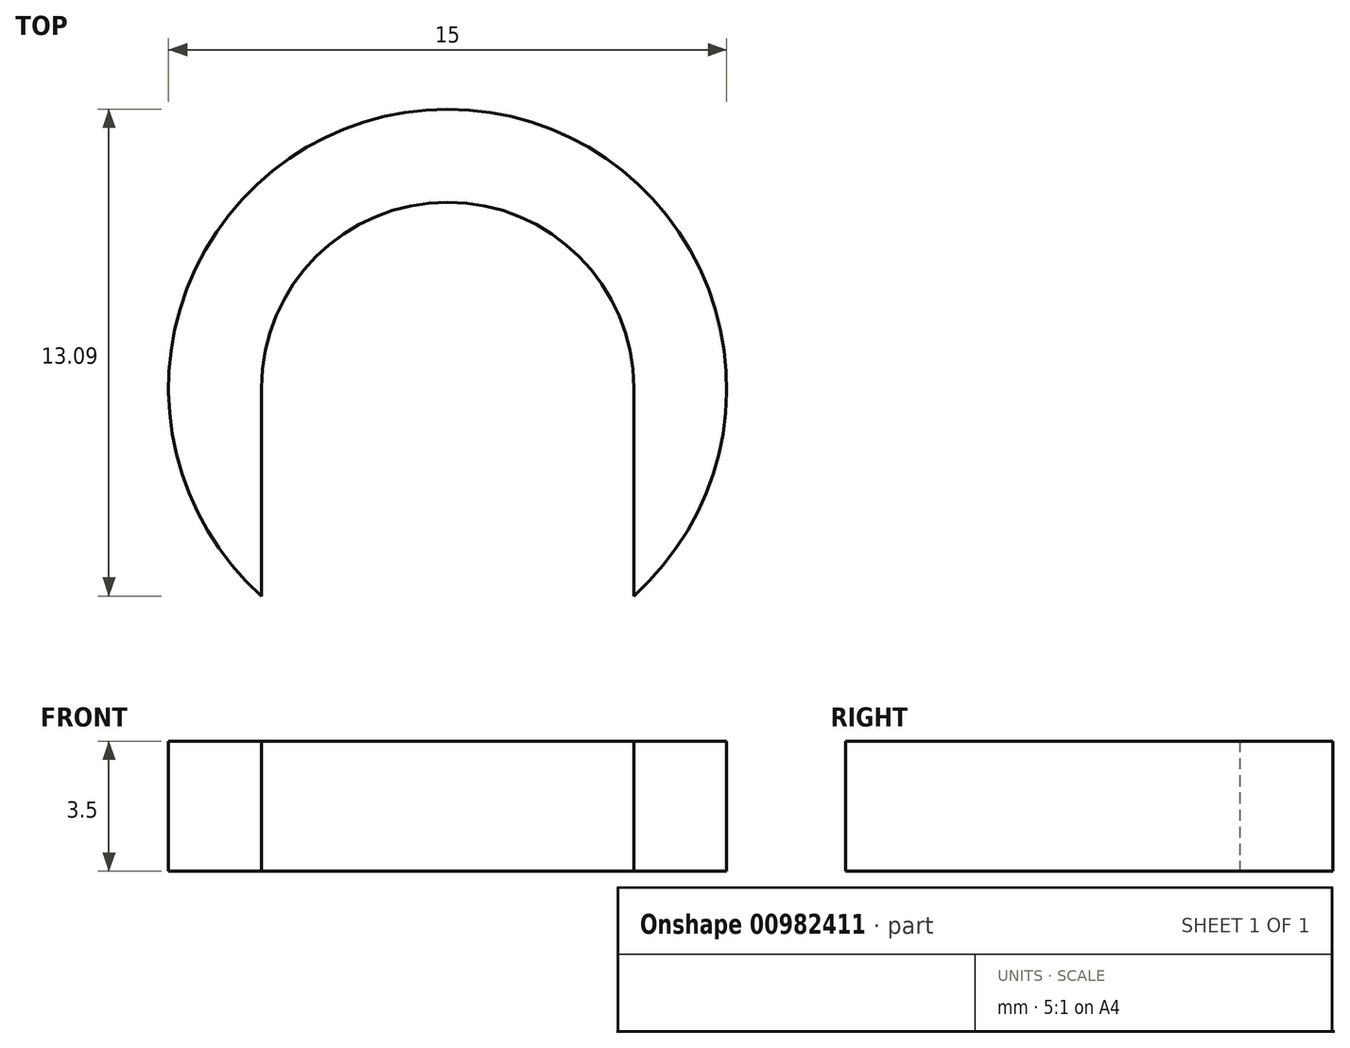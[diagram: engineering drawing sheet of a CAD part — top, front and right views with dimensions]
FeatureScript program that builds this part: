
annotation { "Feature Type Name" : "Feature", "Feature Type Description" : "" }
export const myFeature = defineFeature(function(context is Context, id is Id, definition is map)
    precondition{}
    {
        {
            var Q0;
            Q0=qCreatedBy(makeId("Top.planeOp"),FACE);
            var sketch = newSketch(context, id + "F0", { "sketchPlane" : qUnion([Q0])});
            skCircle(sketch, "E0", {"center": v(0, 0) * mm, "radius": 7.5 * mm});
            skSolve(sketch);
        }
        {
            var Q0;
            Q0=qCreatedBy(makeId("Top.planeOp"),FACE);
            var sketch = newSketch(context, id + "F1", { "sketchPlane" : qUnion([Q0])});
            skLineSegment(sketch, "E1", {"start": v(0, -7.56) * mm, "end": v(-5, -7.56) * mm});
            skLineSegment(sketch, "E2", {"start": v(0, -7.56) * mm, "end": v(5, -7.56) * mm});
            skLineSegment(sketch, "E3", {"start": v(5, -7.56) * mm, "end": v(5, 0) * mm});
            skLineSegment(sketch, "E4", {"start": v(-5, -7.56) * mm, "end": v(-5, 0) * mm});
            skArc(sketch, "E5", {"start": v(5, 0) * mm, "mid": v(0, 5) * mm, "end": v(-5, 0) * mm});
            skSolve(sketch);
        }
        {
            var Q0;
            Q0=makeQuery(id+"F0.imprint","IMPRINT",FACE,{"disambiguationData":[TD([[makeQuery(id+"F0.imprint","IMPRINT",EDGE,{"derivedFrom":sQuery(id+"F0.wireOp",EDGE,"E0")}),1.0]])]});
            extrude(context, id + "F2", {"entities" : qUnion([Q0]), "depth" : 3.5 * mm, "offsetDistance" : 25 * mm});
        }
        {
            var Q0;
            Q0=makeQuery(id+"F1.imprint","IMPRINT",FACE,{"disambiguationData":[TD([[makeQuery(id+"F1.imprint","IMPRINT",EDGE,{"derivedFrom":sQuery(id+"F1.wireOp",EDGE,"E1")}),-1.0]])]});
            extrude(context, id + "F3", {"entities" : qUnion([Q0]), "operationType" : NewBodyOperationType.REMOVE, "depth" : 25 * mm, "offsetDistance" : 25 * mm});
        }
    });
